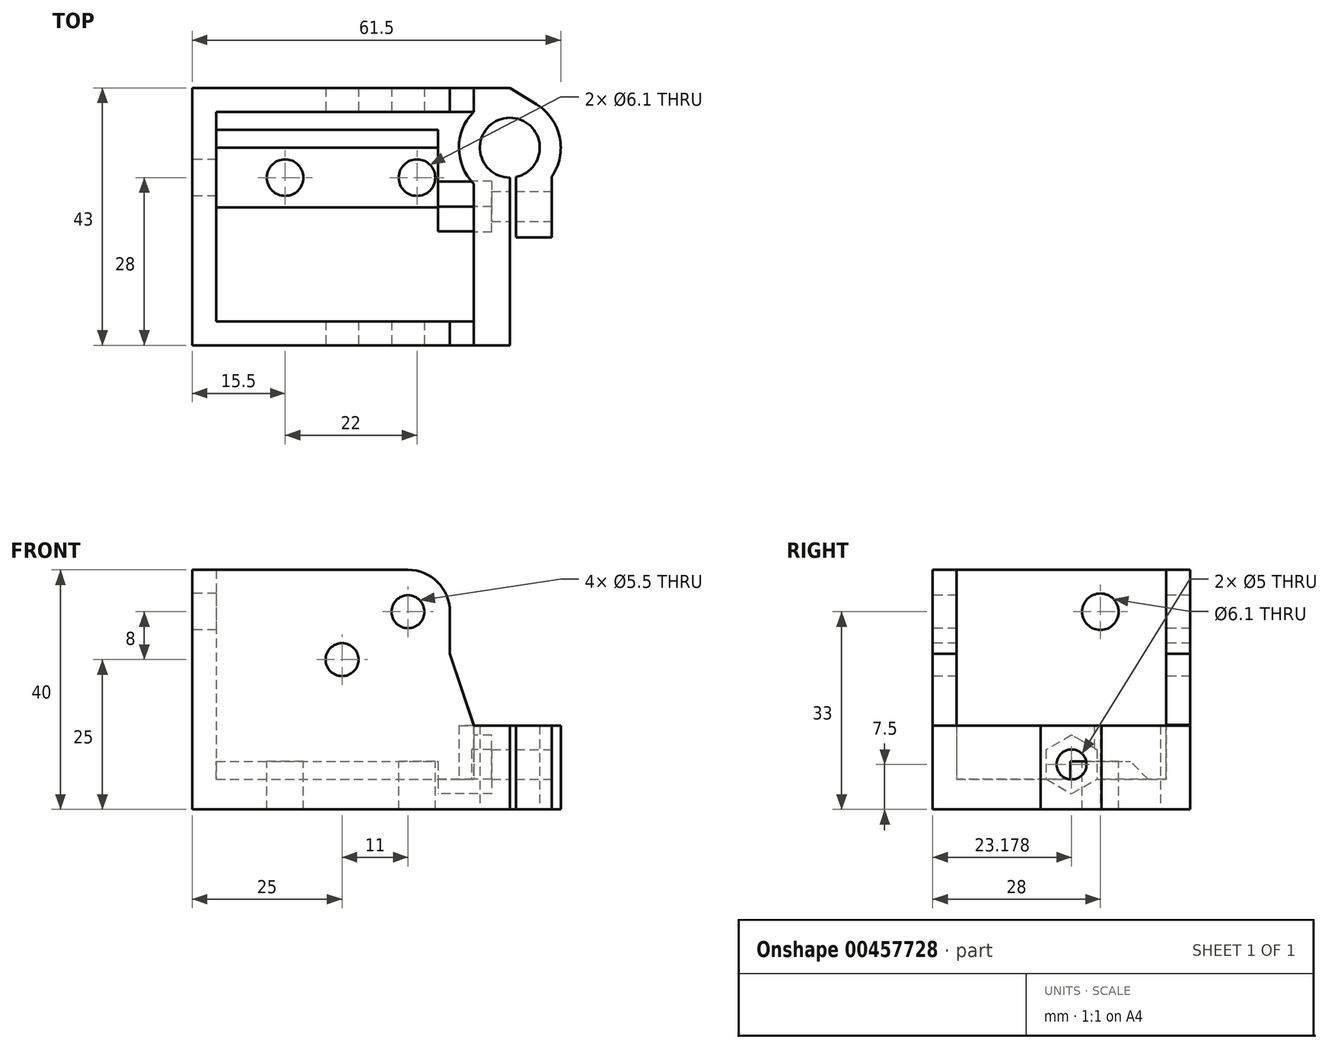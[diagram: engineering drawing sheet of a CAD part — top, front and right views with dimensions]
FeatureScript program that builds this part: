
annotation { "Feature Type Name" : "Feature", "Feature Type Description" : "" }
export const myFeature = defineFeature(function(context is Context, id is Id, definition is map)
    precondition{}
    {
        {
            var Q0;
            Q0=qCreatedBy(makeId("Top.planeOp"),FACE);
            var sketch = newSketch(context, id + "F0", { "sketchPlane" : qUnion([Q0])});
            skLineSegment(sketch, "E0.bottom", {"start": v(0, 0) * mm, "end": v(53, 0) * mm});
            skLineSegment(sketch, "E0.top", {"start": v(0, 43) * mm, "end": v(53, 43) * mm});
            skLineSegment(sketch, "E0.left", {"start": v(0, 0) * mm, "end": v(0, 43) * mm});
            skLineSegment(sketch, "E0.right", {"start": v(53, 0) * mm, "end": v(53, 43) * mm});
            skSolve(sketch);
        }
        {
            var Q0;
            Q0 = qSketchRegion(id + "F0", true);
            extrude(context, id + "F1", {"entities" : qUnion([Q0]), "depth" : 5 * mm});
        }
        {
            var Q0;
            Q0=makeQuery(id+"F1.opExtrude","CAP_FACE",FACE,{"disambiguationData":[OSD([sQuery(id+"F0.wireOp",EDGE,"E0.bottom"),sQuery(id+"F0.wireOp",EDGE,"E0.top"),sQuery(id+"F0.wireOp",EDGE,"E0.left"),sQuery(id+"F0.wireOp",EDGE,"E0.right")])],"isStart":false});
            var sketch = newSketch(context, id + "F2", { "sketchPlane" : qUnion([Q0])});
            skLineSegment(sketch, "E1.bottom", {"start": v(53, 0) * mm, "end": v(47, 0) * mm});
            skLineSegment(sketch, "E1.top", {"start": v(53, 43) * mm, "end": v(47, 43) * mm});
            skLineSegment(sketch, "E1.left", {"start": v(53, 0) * mm, "end": v(53, 24.5) * mm});
            skLineSegment(sketch, "E1.right", {"start": v(47, 0) * mm, "end": v(47, 26.98) * mm});
            skArc(sketch, "E2", {"start": v(54, 28.1) * mm, "mid": v(52.5, 37.97) * mm, "end": v(53, 28) * mm});
            skArc(sketch, "E3", {"start": v(46.9, 38.92) * mm, "mid": v(44.5, 32.93) * mm, "end": v(47, 26.98) * mm});
            skLineSegment(sketch, "E4.top", {"start": v(54, 18) * mm, "end": v(60, 18) * mm});
            skLineSegment(sketch, "E4.left", {"start": v(54, 24.56) * mm, "end": v(54, 18) * mm});
            skLineSegment(sketch, "E4.right", {"start": v(60, 25.8) * mm, "end": v(60, 18) * mm});
            skLineSegment(sketch, "E5", {"start": v(60, 25.8) * mm, "end": v(60, 28.18) * mm});
            skLineSegment(sketch, "E6", {"start": v(53, 43) * mm, "end": v(57.48, 40.23) * mm});
            skArc(sketch, "E7.trimOffspring", {"start": v(60, 28.18) * mm, "mid": v(61.32, 34.74) * mm, "end": v(57.48, 40.23) * mm});
            skLineSegment(sketch, "E8", {"start": v(54, 24.56) * mm, "end": v(54, 28.1) * mm});
            skLineSegment(sketch, "E9", {"start": v(53, 28.1) * mm, "end": v(53, 24.5) * mm});
            skLineSegment(sketch, "E10", {"start": v(46.9, 43) * mm, "end": v(46.9, 38.92) * mm});
            skLineSegment(sketch, "E11", {"start": v(47, 43) * mm, "end": v(46.9, 43) * mm});
            skSolve(sketch);
        }
        {
            var Q0;
            Q0 = qSketchRegion(id + "F2", true);
            extrude(context, id + "F3", {"entities" : qUnion([Q0]), "operationType" : NewBodyOperationType.ADD, "depth" : 9 * mm, "hasSecondDirection" : true, "secondDirectionOppositeDirection" : true, "secondDirectionDepth" : 5 * mm});
        }
        {
            var Q0;
            {var subQ0=sQuery(id+"F2.wireOp",EDGE,"E2");var subQ1=makeQuery(id+"F1.opExtrude","CAP_EDGE",EDGE,{"disambiguationData":[OSD([sQuery(id+"F0.wireOp",EDGE,"E0.right")])],"isStart":false});var subQ2=makeQuery(id+"F2.imprint","INTERSECT",VERTEX,{"disambiguationData":[OD(0.0)],"derivedFrom":[subQ1,subQ0]});Q0=makeQuery(id+"F2.imprint","IMPRINT",FACE,{"disambiguationData":[TD([[makeQuery(id+"F2.imprint","IMPRINT",EDGE,{"disambiguationData":[TD([[subQ2,-1.0]])],"derivedFrom":subQ0}),1.0]])]});}
            extrude(context, id + "F4", {"entities" : qUnion([Q0]), "operationType" : NewBodyOperationType.REMOVE, "oppositeDirection" : true, "depth" : 25 * mm});
        }
        {
            var Q0;
            {var subQ2=sQuery(id+"F2.wireOp",EDGE,"E1.right");Q0=makeQuery(id+"F2.imprint","IMPRINT",FACE,{"disambiguationData":[TD([[makeQuery(id+"F2.imprint","IMPRINT",EDGE,{"derivedFrom":subQ2}),1.0]])]});}
            var sketch = newSketch(context, id + "F5", { "sketchPlane" : qUnion([Q0])});
            skLineSegment(sketch, "E12.bottom", {"start": v(0, 0) * mm, "end": v(47, 0) * mm});
            skLineSegment(sketch, "E12.top", {"start": v(0, 43) * mm, "end": v(46.96, 43) * mm});
            skLineSegment(sketch, "E12.left", {"start": v(0, 0) * mm, "end": v(0, 43) * mm});
            skLineSegment(sketch, "E13.0", {"start": v(4, 39) * mm, "end": v(46.96, 39) * mm});
            skLineSegment(sketch, "E13.1", {"start": v(4, 4) * mm, "end": v(4, 39) * mm});
            skLineSegment(sketch, "E13.2", {"start": v(4, 4) * mm, "end": v(47, 4) * mm});
            skLineSegment(sketch, "E14", {"start": v(47, 0) * mm, "end": v(47, 4) * mm});
            skLineSegment(sketch, "E15", {"start": v(46.96, 43) * mm, "end": v(46.96, 39) * mm});
            skPoint(sketch, "E16.orphan", {"position": v(52.96, 43) * mm});
            skSolve(sketch);
        }
        {
            var Q0;
            Q0 = qSketchRegion(id + "F5", true);
            extrude(context, id + "F6", {"entities" : qUnion([Q0]), "operationType" : NewBodyOperationType.ADD, "depth" : 35 * mm});
        }
        {
            var Q0;
            Q0=makeQuery(id+"F6.boolean.opBoolean","MERGE",FACE,{"derivedFrom":[makeQuery(id+"F3.boolean.opBoolean","MERGE",FACE,{"derivedFrom":[makeQuery(id+"F1.opExtrude","SWEPT_FACE",FACE,{"disambiguationData":[OSD([sQuery(id+"F0.wireOp",EDGE,"E0.bottom")])]}),makeQuery(id+"F3.opExtrude","SWEPT_FACE",FACE,{"disambiguationData":[OSD([sQuery(id+"F2.wireOp",EDGE,"E1.bottom")])]})]}),makeQuery(id+"F6.opExtrude","SWEPT_FACE",FACE,{"disambiguationData":[OSD([sQuery(id+"F5.wireOp",EDGE,"E12.bottom")])]})]});
            var sketch = newSketch(context, id + "F7", { "sketchPlane" : qUnion([Q0])});
            skCircle(sketch, "E17", {"center": v(36, 33) * mm, "radius": 2.75 * mm});
            skCircle(sketch, "E18", {"center": v(25, 25) * mm, "radius": 2.75 * mm});
            skArc(sketch, "E19", {"start": v(43, 33) * mm, "mid": v(40.95, 37.95) * mm, "end": v(36, 40) * mm});
            skLineSegment(sketch, "E20", {"start": v(43, 33) * mm, "end": v(43, 26) * mm});
            skLineSegment(sketch, "E21", {"start": v(43, 26) * mm, "end": v(47, 14) * mm});
            skLineSegment(sketch, "E22", {"start": v(47, 14) * mm, "end": v(47, 40) * mm});
            skLineSegment(sketch, "E23", {"start": v(36, 33) * mm, "end": v(36, 47.95) * mm, "construction": true});
            skLineSegment(sketch, "E24", {"start": v(36, 40) * mm, "end": v(47, 40) * mm});
            skPoint(sketch, "E24.startSnap0", {"position": v(36, 40.48) * mm});
            skSolve(sketch);
        }
        {
            var Q0;
            Q0 = qSketchRegion(id + "F7", true);
            extrude(context, id + "F8", {"entities" : qUnion([Q0]), "operationType" : NewBodyOperationType.REMOVE, "endBound" : BoundingType.THROUGH_ALL, "oppositeDirection" : true, "depth" : 25 * mm});
        }
        {
            var Q0;
            Q0=makeQuery(id+"F3.opExtrude","SWEPT_FACE",FACE,{"disambiguationData":[OSD([sQuery(id+"F2.wireOp",EDGE,"E1.right")])]});
            var sketch = newSketch(context, id + "F9", { "sketchPlane" : qUnion([Q0])});
            skCircle(sketch, "E25.cCircle", {"center": v(-23.18, 7.5) * mm, "radius": 4.25 * mm, "construction": true});
            skLineSegment(sketch, "E25.0", {"start": v(-18.93, 9.95) * mm, "end": v(-18.93, 5.05) * mm});
            skLineSegment(sketch, "E25.1", {"start": v(-18.93, 5.05) * mm, "end": v(-23.18, 2.6) * mm});
            skLineSegment(sketch, "E25.2", {"start": v(-23.18, 2.6) * mm, "end": v(-27.43, 5.05) * mm});
            skLineSegment(sketch, "E25.3", {"start": v(-27.43, 5.05) * mm, "end": v(-27.43, 9.95) * mm});
            skLineSegment(sketch, "E25.4", {"start": v(-27.43, 9.95) * mm, "end": v(-23.18, 12.4) * mm});
            skLineSegment(sketch, "E25.5", {"start": v(-23.18, 12.4) * mm, "end": v(-18.93, 9.95) * mm});
            skPoint(sketch, "E25.0.midPoint", {"position": v(-18.93, 7.5) * mm});
            skSolve(sketch);
        }
        {
            var Q0;
            Q0 = qSketchRegion(id + "F9", true);
            extrude(context, id + "F10", {"entities" : qUnion([Q0]), "operationType" : NewBodyOperationType.REMOVE, "oppositeDirection" : true, "depth" : 3 * mm, "hasSecondDirection" : true, "secondDirectionOppositeDirection" : false, "secondDirectionDepth" : 6 * mm});
        }
        {
            var Q0;
            Q0=makeQuery(id+"F3.opExtrude","SWEPT_FACE",FACE,{"disambiguationData":[OSD([sQuery(id+"F2.wireOp",EDGE,"E4.right"),sQuery(id+"F2.wireOp",EDGE,"E5")])]});
            var sketch = newSketch(context, id + "F11", { "sketchPlane" : qUnion([Q0])});
            skCircle(sketch, "E26", {"center": v(23.18, 7.5) * mm, "radius": 2.5 * mm});
            skSolve(sketch);
        }
        {
            var Q0;
            Q0 = qSketchRegion(id + "F11", true);
            extrude(context, id + "F12", {"entities" : qUnion([Q0]), "operationType" : NewBodyOperationType.REMOVE, "oppositeDirection" : true, "depth" : 25 * mm});
        }
        {
            var Q0;
            {var subQ2=sQuery(id+"F2.wireOp",EDGE,"E1.right");Q0=makeQuery(id+"F2.imprint","IMPRINT",FACE,{"disambiguationData":[TD([[makeQuery(id+"F2.imprint","IMPRINT",EDGE,{"derivedFrom":subQ2}),1.0]])]});}
            var sketch = newSketch(context, id + "F13", { "sketchPlane" : qUnion([Q0])});
            skLineSegment(sketch, "E27.bottom", {"start": v(3.25, 23) * mm, "end": v(41, 23) * mm});
            skLineSegment(sketch, "E27.top", {"start": v(3.25, 33) * mm, "end": v(41, 33) * mm});
            skLineSegment(sketch, "E27.left", {"start": v(3.25, 23) * mm, "end": v(3.25, 33) * mm});
            skLineSegment(sketch, "E27.right", {"start": v(41, 23) * mm, "end": v(41, 33) * mm});
            skSolve(sketch);
        }
        {
            var Q0;
            Q0 = qSketchRegion(id + "F13", true);
            extrude(context, id + "F14", {"entities" : qUnion([Q0]), "operationType" : NewBodyOperationType.ADD, "depth" : 3 * mm});
        }
        {
            var Q0;
            {var subQ2=sQuery(id+"F2.wireOp",EDGE,"E1.right");Q0=makeQuery(id+"F2.imprint","IMPRINT",FACE,{"disambiguationData":[TD([[makeQuery(id+"F2.imprint","IMPRINT",EDGE,{"derivedFrom":subQ2}),1.0]])]});}
            var sketch = newSketch(context, id + "F15", { "sketchPlane" : qUnion([Q0])});
            skCircle(sketch, "E28", {"center": v(15.5, 28) * mm, "radius": 3.05 * mm});
            skCircle(sketch, "E29", {"center": v(37.5, 28) * mm, "radius": 3.05 * mm});
            skSolve(sketch);
        }
        {
            var Q0;
            Q0 = qSketchRegion(id + "F15", true);
            extrude(context, id + "F16", {"entities" : qUnion([Q0]), "operationType" : NewBodyOperationType.REMOVE, "oppositeDirection" : true, "depth" : 25 * mm, "hasSecondDirection" : true, "secondDirectionOppositeDirection" : false, "secondDirectionDepth" : 25 * mm});
        }
        {
            var Q0;
            Q0=makeQuery(id+"F14.opExtrude","CAP_EDGE",EDGE,{"disambiguationData":[OSD([sQuery(id+"F13.wireOp",EDGE,"E27.bottom")])],"isStart":true});
            var Q1;
            Q1=makeQuery(id+"F14.opExtrude","CAP_EDGE",EDGE,{"disambiguationData":[OSD([sQuery(id+"F13.wireOp",EDGE,"E27.top")])],"isStart":true});
            chamfer(context, id + "F17", {"entities" : qUnion([Q0, Q1]), "width" : 3 * mm, "tangentPropagation" : true});
        }
        {
            var Q0;
            Q0=makeQuery(id+"F6.boolean.opBoolean","MERGE",FACE,{"derivedFrom":[makeQuery(id+"F1.opExtrude","SWEPT_FACE",FACE,{"disambiguationData":[OSD([sQuery(id+"F0.wireOp",EDGE,"E0.left")])]}),makeQuery(id+"F6.opExtrude","SWEPT_FACE",FACE,{"disambiguationData":[OSD([sQuery(id+"F5.wireOp",EDGE,"E12.left")])]})]});
            var sketch = newSketch(context, id + "F18", { "sketchPlane" : qUnion([Q0])});
            skCircle(sketch, "E30", {"center": v(-28, 33) * mm, "radius": 3.05 * mm});
            skSolve(sketch);
        }
        {
            var Q0;
            Q0 = qSketchRegion(id + "F18", true);
            extrude(context, id + "F19", {"entities" : qUnion([Q0]), "operationType" : NewBodyOperationType.REMOVE, "oppositeDirection" : true, "depth" : 25 * mm});
        }
    });
